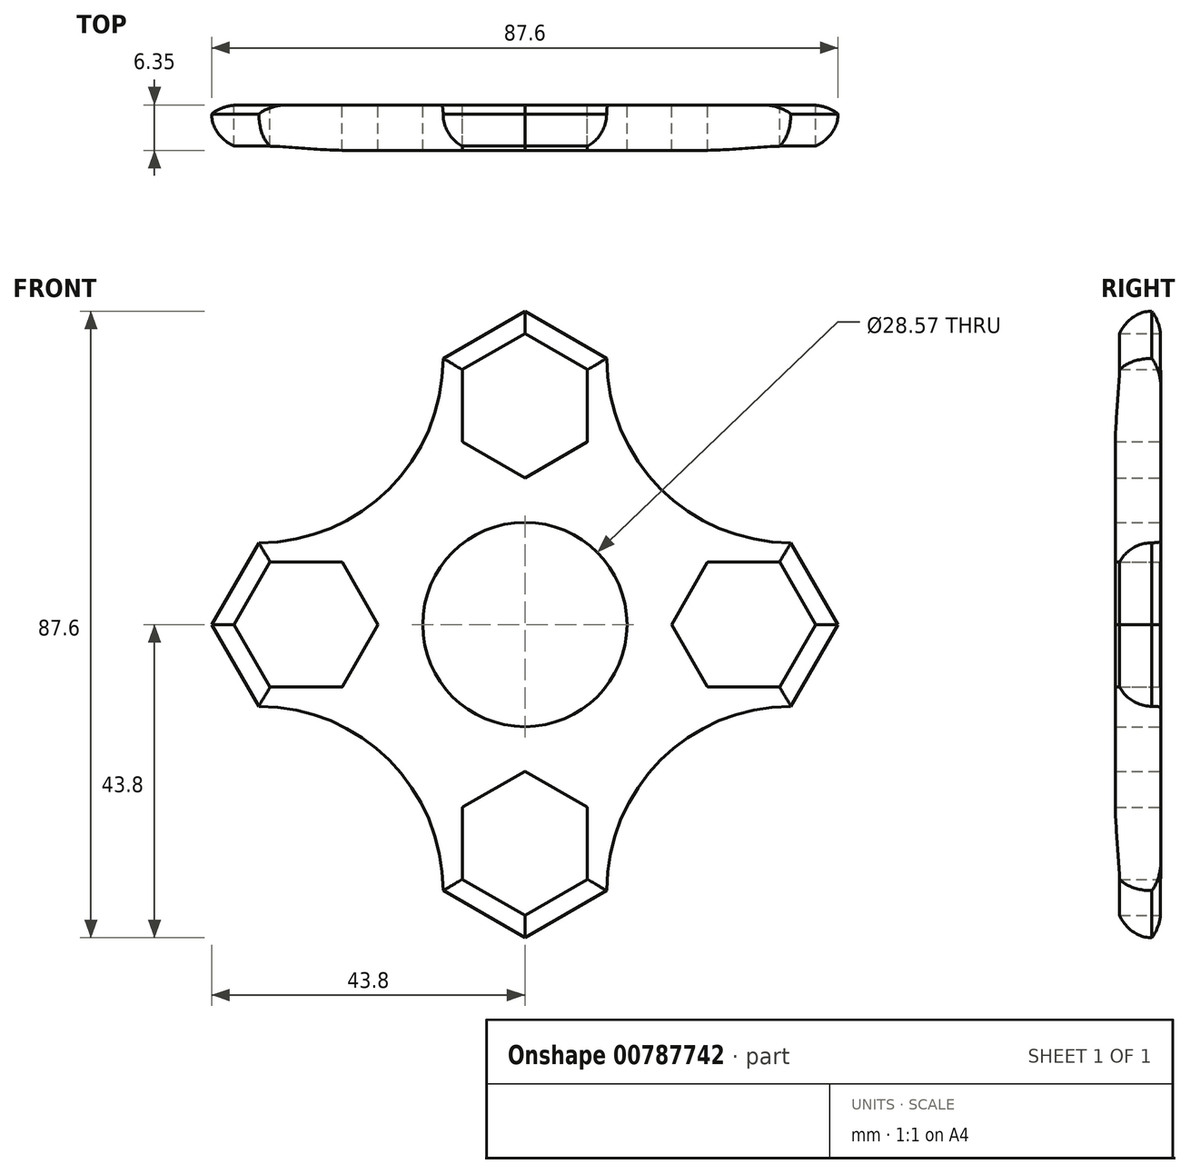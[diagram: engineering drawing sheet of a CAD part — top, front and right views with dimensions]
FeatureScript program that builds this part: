
annotation { "Feature Type Name" : "Feature", "Feature Type Description" : "" }
export const myFeature = defineFeature(function(context is Context, id is Id, definition is map)
    precondition{}
    {
        {
            var Q0;
            Q0=qCreatedBy(makeId("Front.planeOp"),FACE);
            var sketch = newSketch(context, id + "F0", { "sketchPlane" : qUnion([Q0])});
            skCircle(sketch, "E0", {"center": v(0, 0) * mm, "radius": 14.29 * mm});
            skCircle(sketch, "E1", {"center": v(0, 0) * mm, "radius": 11.02 * mm});
            skCircle(sketch, "E2.cCircle", {"center": v(0, 30.6) * mm, "radius": 8.74 * mm, "construction": true});
            skLineSegment(sketch, "E2.0", {"start": v(-8.74, 25.56) * mm, "end": v(-8.74, 35.65) * mm});
            skLineSegment(sketch, "E2.1", {"start": v(-8.74, 35.65) * mm, "end": v(0, 40.7) * mm});
            skLineSegment(sketch, "E2.2", {"start": v(0, 40.7) * mm, "end": v(8.74, 35.65) * mm});
            skLineSegment(sketch, "E2.3", {"start": v(8.74, 35.65) * mm, "end": v(8.74, 25.56) * mm});
            skLineSegment(sketch, "E2.4", {"start": v(8.74, 25.56) * mm, "end": v(0, 20.51) * mm});
            skLineSegment(sketch, "E2.5", {"start": v(0, 20.51) * mm, "end": v(-8.74, 25.56) * mm});
            skPoint(sketch, "E2.0.midPoint", {"position": v(-8.74, 30.6) * mm});
            skCircle(sketch, "E3.cCircle", {"center": v(0, 30.6) * mm, "radius": 11.43 * mm, "construction": true});
            skLineSegment(sketch, "E3.0", {"start": v(-11.43, 24) * mm, "end": v(-11.43, 37.2) * mm});
            skLineSegment(sketch, "E3.1", {"start": v(-11.43, 37.2) * mm, "end": v(0, 43.8) * mm});
            skLineSegment(sketch, "E3.2", {"start": v(0, 43.8) * mm, "end": v(11.43, 37.2) * mm});
            skLineSegment(sketch, "E3.3", {"start": v(11.43, 37.2) * mm, "end": v(11.43, 24) * mm});
            skLineSegment(sketch, "E3.4", {"start": v(11.43, 24) * mm, "end": v(0, 17.4) * mm});
            skLineSegment(sketch, "E3.5", {"start": v(0, 17.4) * mm, "end": v(-11.43, 24) * mm});
            skPoint(sketch, "E3.0.midPoint", {"position": v(-11.43, 30.6) * mm});
            skPoint(sketch, "E4.1.0", {"position": v(-30.6, -8.74) * mm});
            skLineSegment(sketch, "E4.1.1", {"start": v(-43.8, 0) * mm, "end": v(-37.2, 11.43) * mm});
            skLineSegment(sketch, "E4.1.2", {"start": v(-37.2, -11.43) * mm, "end": v(-43.8, 0) * mm});
            skLineSegment(sketch, "E4.1.3", {"start": v(-24, -11.43) * mm, "end": v(-37.2, -11.43) * mm});
            skCircle(sketch, "E4.1.4", {"center": v(-30.6, 0) * mm, "radius": 11.43 * mm, "construction": true});
            skLineSegment(sketch, "E4.1.5", {"start": v(-20.51, 0) * mm, "end": v(-25.56, -8.74) * mm});
            skLineSegment(sketch, "E4.1.6", {"start": v(-25.56, 8.74) * mm, "end": v(-20.51, 0) * mm});
            skLineSegment(sketch, "E4.1.7", {"start": v(-35.65, 8.74) * mm, "end": v(-25.56, 8.74) * mm});
            skLineSegment(sketch, "E4.1.8", {"start": v(-40.7, 0) * mm, "end": v(-35.65, 8.74) * mm});
            skLineSegment(sketch, "E4.1.9", {"start": v(-37.2, 11.43) * mm, "end": v(-24, 11.43) * mm});
            skLineSegment(sketch, "E4.1.10", {"start": v(-24, 11.43) * mm, "end": v(-17.4, 0) * mm});
            skLineSegment(sketch, "E4.1.11", {"start": v(-17.4, 0) * mm, "end": v(-24, -11.43) * mm});
            skPoint(sketch, "E4.1.12", {"position": v(-30.6, -11.43) * mm});
            skCircle(sketch, "E4.1.13", {"center": v(-30.6, 0) * mm, "radius": 8.74 * mm, "construction": true});
            skLineSegment(sketch, "E4.1.14", {"start": v(-25.56, -8.74) * mm, "end": v(-35.65, -8.74) * mm});
            skLineSegment(sketch, "E4.1.15", {"start": v(-35.65, -8.74) * mm, "end": v(-40.7, 0) * mm});
            skLineSegment(sketch, "E5.1.2.0", {"start": v(0, -43.8) * mm, "end": v(-11.43, -37.2) * mm});
            skLineSegment(sketch, "E5.4.2.0", {"start": v(11.43, -37.2) * mm, "end": v(0, -43.8) * mm});
            skLineSegment(sketch, "E5.7.2.0", {"start": v(11.43, -24) * mm, "end": v(11.43, -37.2) * mm});
            skPoint(sketch, "E5.8.2.0", {"position": v(8.74, -30.6) * mm});
            skCircle(sketch, "E5.10.2.0", {"center": v(0, -30.6) * mm, "radius": 11.43 * mm, "construction": true});
            skLineSegment(sketch, "E5.12.2.0", {"start": v(0, -20.51) * mm, "end": v(8.74, -25.56) * mm});
            skLineSegment(sketch, "E5.15.2.0", {"start": v(-8.74, -25.56) * mm, "end": v(0, -20.51) * mm});
            skLineSegment(sketch, "E5.18.2.0", {"start": v(-8.74, -35.65) * mm, "end": v(-8.74, -25.56) * mm});
            skLineSegment(sketch, "E5.21.2.0", {"start": v(0, -40.7) * mm, "end": v(-8.74, -35.65) * mm});
            skLineSegment(sketch, "E5.24.2.0", {"start": v(-11.43, -37.2) * mm, "end": v(-11.43, -24) * mm});
            skLineSegment(sketch, "E5.27.2.0", {"start": v(-11.43, -24) * mm, "end": v(0, -17.4) * mm});
            skLineSegment(sketch, "E5.30.2.0", {"start": v(0, -17.4) * mm, "end": v(11.43, -24) * mm});
            skPoint(sketch, "E5.33.2.0", {"position": v(11.43, -30.6) * mm});
            skCircle(sketch, "E5.34.2.0", {"center": v(0, -30.6) * mm, "radius": 8.74 * mm, "construction": true});
            skLineSegment(sketch, "E5.36.2.0", {"start": v(8.74, -25.56) * mm, "end": v(8.74, -35.65) * mm});
            skLineSegment(sketch, "E5.39.2.0", {"start": v(8.74, -35.65) * mm, "end": v(0, -40.7) * mm});
            skLineSegment(sketch, "E6.1.3.0", {"start": v(43.8, 0) * mm, "end": v(37.2, -11.43) * mm});
            skLineSegment(sketch, "E6.4.3.0", {"start": v(37.2, 11.43) * mm, "end": v(43.8, 0) * mm});
            skLineSegment(sketch, "E6.7.3.0", {"start": v(24, 11.43) * mm, "end": v(37.2, 11.43) * mm});
            skPoint(sketch, "E6.8.3.0", {"position": v(30.6, 8.74) * mm});
            skCircle(sketch, "E6.10.3.0", {"center": v(30.6, 0) * mm, "radius": 11.43 * mm, "construction": true});
            skLineSegment(sketch, "E6.12.3.0", {"start": v(20.51, 0) * mm, "end": v(25.56, 8.74) * mm});
            skLineSegment(sketch, "E6.15.3.0", {"start": v(25.56, -8.74) * mm, "end": v(20.51, 0) * mm});
            skLineSegment(sketch, "E6.18.3.0", {"start": v(35.65, -8.74) * mm, "end": v(25.56, -8.74) * mm});
            skLineSegment(sketch, "E6.21.3.0", {"start": v(40.7, 0) * mm, "end": v(35.65, -8.74) * mm});
            skLineSegment(sketch, "E6.24.3.0", {"start": v(37.2, -11.43) * mm, "end": v(24, -11.43) * mm});
            skLineSegment(sketch, "E6.27.3.0", {"start": v(24, -11.43) * mm, "end": v(17.4, 0) * mm});
            skLineSegment(sketch, "E6.30.3.0", {"start": v(17.4, 0) * mm, "end": v(24, 11.43) * mm});
            skPoint(sketch, "E6.33.3.0", {"position": v(30.6, 11.43) * mm});
            skCircle(sketch, "E6.34.3.0", {"center": v(30.6, 0) * mm, "radius": 8.74 * mm, "construction": true});
            skLineSegment(sketch, "E6.36.3.0", {"start": v(25.56, 8.74) * mm, "end": v(35.65, 8.74) * mm});
            skLineSegment(sketch, "E6.39.3.0", {"start": v(35.65, 8.74) * mm, "end": v(40.7, 0) * mm});
            skArc(sketch, "E7", {"start": v(-37.2, 11.43) * mm, "mid": v(-18.98, 18.98) * mm, "end": v(-11.43, 37.2) * mm});
            skArc(sketch, "E8", {"start": v(11.43, 37.2) * mm, "mid": v(18.98, 18.98) * mm, "end": v(37.2, 11.43) * mm});
            skArc(sketch, "E9", {"start": v(37.2, -11.43) * mm, "mid": v(18.98, -18.98) * mm, "end": v(11.43, -37.2) * mm});
            skArc(sketch, "E10", {"start": v(-11.43, -37.2) * mm, "mid": v(-18.98, -18.98) * mm, "end": v(-37.2, -11.43) * mm});
            skSolve(sketch);
        }
        {
            var Q0;
            Q0 = qSketchRegion(id + "F0", true);
            extrude(context, id + "F1", {"entities" : qUnion([Q0]), "depth" : 6.35 * mm, "offsetDistance" : 25.4 * mm});
        }
        {
            var Q0;
            Q0=makeQuery(id+"F1.opExtrude","CAP_EDGE",EDGE,{"disambiguationData":[OSD([sQuery(id+"F0.wireOp",EDGE,"E3.2")])],"isStart":false});
            var Q1;
            Q1=makeQuery(id+"F1.opExtrude","CAP_EDGE",EDGE,{"disambiguationData":[OSD([sQuery(id+"F0.wireOp",EDGE,"E3.1")])],"isStart":false});
            var Q2;
            Q2=makeQuery(id+"F1.opExtrude","CAP_EDGE",EDGE,{"disambiguationData":[OSD([sQuery(id+"F0.wireOp",EDGE,"E6.4.3.0")])],"isStart":false});
            var Q3;
            Q3=makeQuery(id+"F1.opExtrude","CAP_EDGE",EDGE,{"disambiguationData":[OSD([sQuery(id+"F0.wireOp",EDGE,"E6.1.3.0")])],"isStart":false});
            var Q4;
            Q4=makeQuery(id+"F1.opExtrude","CAP_EDGE",EDGE,{"disambiguationData":[OSD([sQuery(id+"F0.wireOp",EDGE,"E5.4.2.0")])],"isStart":false});
            var Q5;
            Q5=makeQuery(id+"F1.opExtrude","CAP_EDGE",EDGE,{"disambiguationData":[OSD([sQuery(id+"F0.wireOp",EDGE,"E5.1.2.0")])],"isStart":false});
            var Q6;
            Q6=makeQuery(id+"F1.opExtrude","CAP_EDGE",EDGE,{"disambiguationData":[OSD([sQuery(id+"F0.wireOp",EDGE,"E4.1.2")])],"isStart":false});
            var Q7;
            Q7=makeQuery(id+"F1.opExtrude","CAP_EDGE",EDGE,{"disambiguationData":[OSD([sQuery(id+"F0.wireOp",EDGE,"E4.1.1")])],"isStart":false});
            fillet(context, id + "F2", {"entities" : qUnion([Q0, Q1, Q2, Q3, Q4, Q5, Q6, Q7]), "radius" : 5.08 * mm, "tangentPropagation" : true, "allowEdgeOverflow" : false});
        }
        {
            var Q0;
            Q0=makeQuery(id+"F1.opExtrude","CAP_EDGE",EDGE,{"disambiguationData":[OSD([sQuery(id+"F0.wireOp",EDGE,"E3.2")])],"isStart":true});
            var Q1;
            Q1=makeQuery(id+"F1.opExtrude","CAP_EDGE",EDGE,{"disambiguationData":[OSD([sQuery(id+"F0.wireOp",EDGE,"E3.1")])],"isStart":true});
            var Q2;
            Q2=makeQuery(id+"F1.opExtrude","CAP_EDGE",EDGE,{"disambiguationData":[OSD([sQuery(id+"F0.wireOp",EDGE,"E4.1.1")])],"isStart":true});
            var Q3;
            Q3=makeQuery(id+"F1.opExtrude","CAP_EDGE",EDGE,{"disambiguationData":[OSD([sQuery(id+"F0.wireOp",EDGE,"E4.1.2")])],"isStart":true});
            var Q4;
            Q4=makeQuery(id+"F1.opExtrude","CAP_EDGE",EDGE,{"disambiguationData":[OSD([sQuery(id+"F0.wireOp",EDGE,"E5.1.2.0")])],"isStart":true});
            var Q5;
            Q5=makeQuery(id+"F1.opExtrude","CAP_EDGE",EDGE,{"disambiguationData":[OSD([sQuery(id+"F0.wireOp",EDGE,"E5.4.2.0")])],"isStart":true});
            var Q6;
            Q6=makeQuery(id+"F1.opExtrude","CAP_EDGE",EDGE,{"disambiguationData":[OSD([sQuery(id+"F0.wireOp",EDGE,"E6.4.3.0")])],"isStart":true});
            var Q7;
            Q7=makeQuery(id+"F1.opExtrude","CAP_EDGE",EDGE,{"disambiguationData":[OSD([sQuery(id+"F0.wireOp",EDGE,"E6.1.3.0")])],"isStart":true});
            fillet(context, id + "F3", {"entities" : qUnion([Q0, Q1, Q2, Q3, Q4, Q5, Q6, Q7]), "radius" : 5.08 * mm, "tangentPropagation" : true, "allowEdgeOverflow" : false});
        }
        {
            var Q0;
            Q0=makeQuery(id+"F1.opExtrude","CAP_EDGE",EDGE,{"disambiguationData":[OSD([sQuery(id+"F0.wireOp",EDGE,"E8")])],"isStart":false});
            var Q1;
            Q1=makeQuery(id+"F1.opExtrude","CAP_EDGE",EDGE,{"disambiguationData":[OSD([sQuery(id+"F0.wireOp",EDGE,"E9")])],"isStart":false});
            var Q2;
            Q2=makeQuery(id+"F1.opExtrude","CAP_EDGE",EDGE,{"disambiguationData":[OSD([sQuery(id+"F0.wireOp",EDGE,"E10")])],"isStart":false});
            var Q3;
            Q3=makeQuery(id+"F1.opExtrude","CAP_EDGE",EDGE,{"disambiguationData":[OSD([sQuery(id+"F0.wireOp",EDGE,"E7")])],"isStart":false});
            fillet(context, id + "F4", {"entities" : qUnion([Q0, Q1, Q2, Q3]), "radius" : 5.08 * mm, "tangentPropagation" : true, "allowEdgeOverflow" : false});
        }
    });
